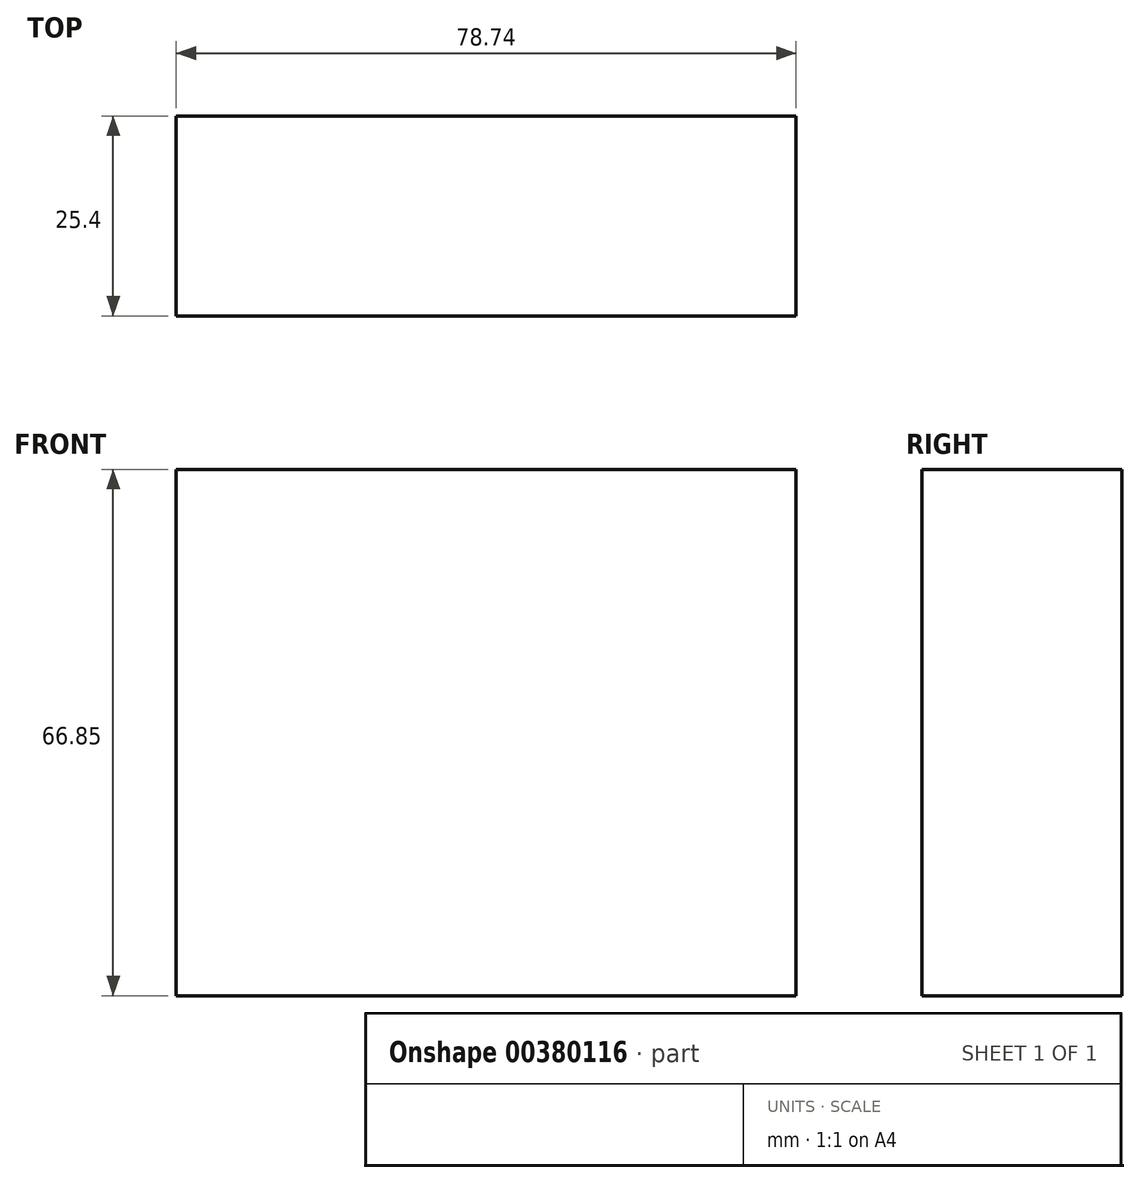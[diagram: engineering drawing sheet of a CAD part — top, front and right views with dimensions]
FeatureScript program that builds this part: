
annotation { "Feature Type Name" : "Feature", "Feature Type Description" : "" }
export const myFeature = defineFeature(function(context is Context, id is Id, definition is map)
    precondition{}
    {
        {
            var Q0;
            Q0=qCreatedBy(makeId("Front.planeOp"),FACE);
            var sketch = newSketch(context, id + "F0", { "sketchPlane" : qUnion([Q0])});
            skLineSegment(sketch, "E0.bottom", {"start": v(-35.56, 21.23) * mm, "end": v(43.18, 21.23) * mm});
            skLineSegment(sketch, "E0.top", {"start": v(-35.56, -45.62) * mm, "end": v(43.18, -45.62) * mm});
            skLineSegment(sketch, "E0.left", {"start": v(-35.56, 21.23) * mm, "end": v(-35.56, -45.62) * mm});
            skLineSegment(sketch, "E0.right", {"start": v(43.18, 21.23) * mm, "end": v(43.18, -45.62) * mm});
            skSolve(sketch);
        }
        {
            var Q0;
            Q0 = qSketchRegion(id + "F0", true);
            extrude(context, id + "F1", {"entities" : qUnion([Q0]), "depth" : 25.4 * mm});
        }
    });
